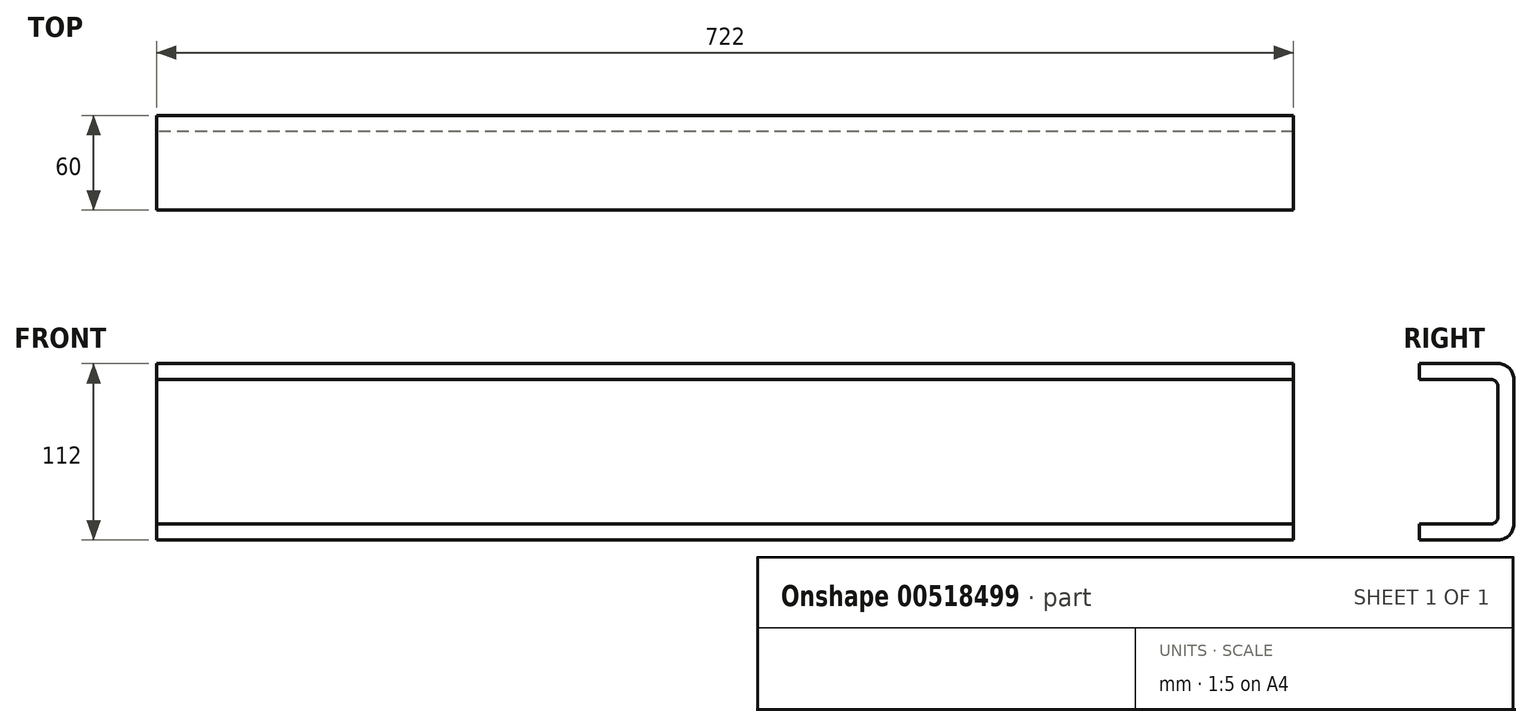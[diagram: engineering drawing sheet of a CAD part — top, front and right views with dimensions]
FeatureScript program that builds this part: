
annotation { "Feature Type Name" : "Feature", "Feature Type Description" : "" }
export const myFeature = defineFeature(function(context is Context, id is Id, definition is map)
    precondition{}
    {
        {
            var Q0;
            Q0=qCreatedBy(makeId("Right.planeOp"),FACE);
            var sketch = newSketch(context, id + "F0", { "sketchPlane" : qUnion([Q0])});
            skLineSegment(sketch, "E0", {"start": v(0, 0) * mm, "end": v(50, 0) * mm});
            skLineSegment(sketch, "E1", {"start": v(60, -10) * mm, "end": v(60, -102) * mm});
            skLineSegment(sketch, "E2", {"start": v(50, -112) * mm, "end": v(0, -112) * mm});
            skLineSegment(sketch, "E3", {"start": v(0, -112) * mm, "end": v(0, -102) * mm});
            skLineSegment(sketch, "E4", {"start": v(0, -102) * mm, "end": v(45, -102) * mm});
            skLineSegment(sketch, "E5", {"start": v(50, -97) * mm, "end": v(50, -15) * mm});
            skLineSegment(sketch, "E6", {"start": v(45, -10) * mm, "end": v(0, -10) * mm});
            skLineSegment(sketch, "E7", {"start": v(0, -10) * mm, "end": v(0, 0) * mm});
            skPoint(sketch, "E8.visualSharp", {"position": v(60, 0) * mm});
            skArc(sketch, "E8.filletArc", {"start": v(60, -10) * mm, "mid": v(57.07, -2.93) * mm, "end": v(50, 0) * mm});
            skArc(sketch, "E9.filletArc", {"start": v(50, -15) * mm, "mid": v(48.54, -11.46) * mm, "end": v(45, -10) * mm});
            skPoint(sketch, "E10.visualSharp", {"position": v(50, -102) * mm});
            skArc(sketch, "E10.filletArc", {"start": v(45, -102) * mm, "mid": v(48.54, -100.54) * mm, "end": v(50, -97) * mm});
            skPoint(sketch, "E11.visualSharp", {"position": v(60, -112) * mm});
            skArc(sketch, "E11.filletArc", {"start": v(50, -112) * mm, "mid": v(57.07, -109.07) * mm, "end": v(60, -102) * mm});
            skSolve(sketch);
        }
        {
            var Q0;
            Q0 = qSketchRegion(id + "F0", true);
            extrude(context, id + "F1", {"entities" : qUnion([Q0]), "endBound" : BoundingType.SYMMETRIC, "depth" : 722 * mm, "offsetDistance" : 25 * mm});
        }
    });
